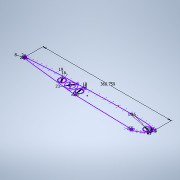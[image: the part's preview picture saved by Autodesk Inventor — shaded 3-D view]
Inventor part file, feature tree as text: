
AUTODESK INVENTOR PART (.ipt)
format: ipt  version: 2022 (Build 260153000, 153)  size: 202,752 bytes
history: native  units: mm
features: sketch x1
ambient origin geometry x8: Origin, YZ Plane, XZ Plane, XY Plane, X Axis, Y Axis, Z Axis, Center Point
feature tree (1):
  sketch  "Sketch1"  dims[d31=34.456mm d50=368.759386mm d57=16.0mm d69=8.0mm d70=23.0mm d71=8.0mm d73=16.0mm d80=19.0mm d81=16.0mm d82=1.0mm d83=1.0mm d84=1.0mm d85=1.0mm d86=1.0mm d87=0.8mm d88=1.0mm d90=19.0mm d94=5.0mm d95=5.0mm d105=5.0mm d106=5.0mm d108=2.0mm d109=19.0mm d114=5.0mm d115=5.0mm]
